# Revit family: PANZERI_HILOW_WALL_LIGHT
name_source: partatom
category: Lighting Fixtures
revit_build: Autodesk Revit 2018 (Build: 20190510_1515(x64)
units: mm (PartAtom-declared; Revit-internal decimal feet)

## family parameters
Cut with Voids When Loaded = No
Host = Face
Light Source = Yes
OmniClass Number = 23.80.70.00
OmniClass Title = Lighting
Part Type = Normal
Room Calculation Point = Yes
Round Connector Dimension = Use Diameter
Shared = No

## types (2) — shared parameters
AVAILABLE FINISHES = Structure: white, mat black, bronze, mat brass or titanium; Diffusers: Opaline or black screen. CUSTOM finishes available only on request.
Apparent Load = 0 VA
BIM BADGE = https://bim.archiproducts.com
CANOPY MATERIAL = PANZERI_ALUMINIUM_POLYACRYLIC_PAINT_MAT_BRASS_19
COLLECTION = HILOW
COLOR RENDERING INDEX = Ra>90
Color Filter = 16777215
DEPTH = 820 mm
DESIGNER = Matteo Thun
Default Elevation = 1219 mm
Description = Wall lighting fixture for interiors, with direct and indirect light emission. ‎
Dimming Lamp Color Temperature Shift = <None>
ENERGY EFFICIENCY CLASS = N/D
FREQUENCY = 0 Hz
HEIGHT = 130 mm
INSTALLATION INSTRUCTIONS = https://panzeri.it
IP RATING = IP20
LAMP MATERIAL = PANZERI_POLYCARBONATE_BLACK_SCREEN_Light_on
Lamp = LED
Light Source Symbol Size = 300 mm
MATERIAL DESCRIPTION = Pickled sheet metal wall bracket in polyacrylic paint. Pickled sheet metal wall plate in polyacrylic paint. Extruded aluminium structure in polyacrylic paint.
Joints in turned brass and die-cast aluminium in polyacrylic paint. Die-cast aluminium end caps in polyacrylic paint. Extruded polycarbonate diffusers with black finish for direct light emission and opaline finish for indirect light emission.
Manufacturer = PANZERI
Model = HILOW WALL
PACKAGING = 87,0 x 118,0 x 14,0 cm
PRODUCT SHEET = https://www.archiproducts.com
STRUCTURE MATERIAL = PANZERI_ALUMINIUM_POLYACRYLIC_PAINT_MAT_BRASS_19
TECHNICAL SHEET = https://panzeri.it
Tilt Angle = -90.00°
URL = https://panzeri.it
USAGE = INDOOR - WALL
VOLTAGE = 0 V
WIDTH = 1130 mm

## per-type parameters (varying)
| type | ACCESSORIES | CANOPY_LENGTH | COMPOSITIONS | FREQUENCY RANGE | LIGHTING SPECIFICATION | POWER SUPPLY | PRODUCT CODE | Photometric Web File | SINGLE INSTALLATION | Type Comments | WATTAGE | WEIGHT |
| Single_BlackScreen_MatBrass | DRIVER: integrated included | 320 mm | No | 50/60Hz | LED 77W / 2700K / Ra>90 / 3812lm / 220-240V AC / dimmable (DALI /Push DIM) | 220-240V AC | A02919.115.0502 | Hilow black wall A029__.115.0502 - 8064.IES | Yes | Direct and indirect light emission. For single installations. | 77 W | 2.97 kg |
| Compositions_BlackScreen_MatBrass | DRIVER: remote not included | 100 mm | Yes |  | LED 71W / 2700K / Ra>90 / 4088lm / 24V DC | 24V DC | A02919.115.0510 | Hilow black wall A029__.115.0510 - 8568.IES | No | Direct and indirect light emission. For compositions. | 71 W | 2.15 kg |

## geometry (parser evidence)
native form markers: Sweep x5
no freeform markers — native parametric forms only
